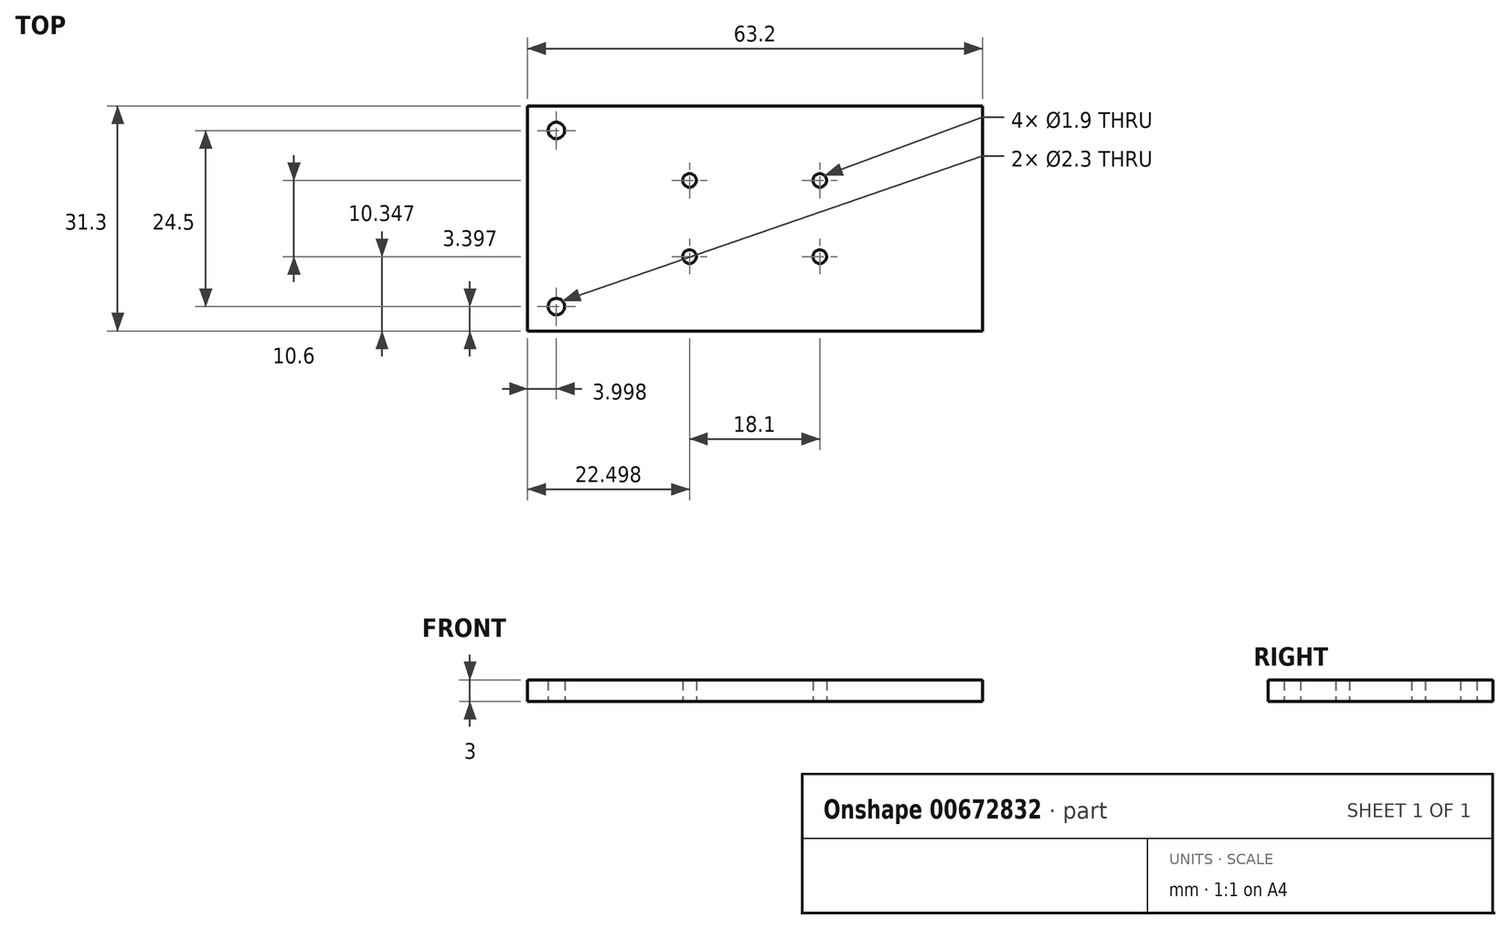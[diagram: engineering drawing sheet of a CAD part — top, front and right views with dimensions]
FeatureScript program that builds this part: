
annotation { "Feature Type Name" : "Feature", "Feature Type Description" : "" }
export const myFeature = defineFeature(function(context is Context, id is Id, definition is map)
    precondition{}
    {
        {
            var Q0;
            Q0=qCreatedBy(makeId("Top.planeOp"),FACE);
            var sketch = newSketch(context, id + "F0", { "sketchPlane" : qUnion([Q0])});
            skLineSegment(sketch, "E0.bottom", {"start": v(-37.93, -0.11) * mm, "end": v(25.27, -0.11) * mm});
            skLineSegment(sketch, "E0.top", {"start": v(-37.93, -15.76) * mm, "end": v(25.27, -15.76) * mm});
            skLineSegment(sketch, "E0.left", {"start": v(-37.93, -0.11) * mm, "end": v(-37.93, -15.76) * mm});
            skLineSegment(sketch, "E0.right", {"start": v(25.27, -0.11) * mm, "end": v(25.27, -15.76) * mm});
            skLineSegment(sketch, "E1", {"start": v(-33.93, -0.11) * mm, "end": v(-33.93, -3.51) * mm});
            skLineSegment(sketch, "E2", {"start": v(-33.93, -3.51) * mm, "end": v(-37.93, -3.51) * mm});
            skCircle(sketch, "E3", {"center": v(-33.93, -3.51) * mm, "radius": 1.15 * mm});
            skLineSegment(sketch, "E4", {"start": v(-37.93, -10.46) * mm, "end": v(-15.43, -10.46) * mm});
            skLineSegment(sketch, "E5", {"start": v(-15.43, -10.46) * mm, "end": v(2.67, -10.46) * mm});
            skLineSegment(sketch, "E6", {"start": v(-5.3, -10.46) * mm, "end": v(-5.3, -15.76) * mm});
            skCircle(sketch, "E7", {"center": v(-15.43, -10.46) * mm, "radius": 0.95 * mm});
            skCircle(sketch, "E8", {"center": v(2.67, -10.46) * mm, "radius": 0.95 * mm});
            skSolve(sketch);
        }
        {
            var Q0;
            {var subQ13=sQuery(id+"F0.wireOp",EDGE,"E0.right");Q0=makeQuery(id+"F0.imprint","IMPRINT",FACE,{"disambiguationData":[TD([[makeQuery(id+"F0.imprint","IMPRINT",EDGE,{"derivedFrom":subQ13}),-1.0]])]});}
            var Q1;
            {var subQ1=sQuery(id+"F0.wireOp",EDGE,"E0.left");var subQ5=sQuery(id+"F0.wireOp",EDGE,"E0.bottom");var subQ6=makeQuery(id+"F0.imprint","INTERSECT",VERTEX,{"derivedFrom":[subQ5,subQ1]});Q1=makeQuery(id+"F0.imprint","IMPRINT",FACE,{"disambiguationData":[TD([[makeQuery(id+"F0.imprint","IMPRINT",EDGE,{"disambiguationData":[TD([[subQ6,-1.0]])],"derivedFrom":subQ5}),-1.0]])]});}
            var Q2;
            {var subQ7=sQuery(id+"F0.wireOp",EDGE,"E6");Q2=makeQuery(id+"F0.imprint","IMPRINT",FACE,{"disambiguationData":[TD([[makeQuery(id+"F0.imprint","IMPRINT",EDGE,{"derivedFrom":subQ7}),-1.0]])]});}
            extrude(context, id + "F1", {"entities" : qUnion([Q0, Q1, Q2]), "depth" : 3 * mm, "offsetDistance" : 25 * mm});
        }
        {
            var Q0;
            Q0=makeQuery(id+"F1.opExtrude","SWEPT_BODY",BODY,{"disambiguationData":[OSD([sQuery(id+"F0.wireOp",EDGE,"E0.bottom"),sQuery(id+"F0.wireOp",EDGE,"E0.top"),sQuery(id+"F0.wireOp",EDGE,"E0.left"),sQuery(id+"F0.wireOp",EDGE,"E0.right"),sQuery(id+"F0.wireOp",EDGE,"E3"),sQuery(id+"F0.wireOp",EDGE,"E7"),sQuery(id+"F0.wireOp",EDGE,"E8")])]});
            var Q1;
            Q1=makeQuery(id+"F1.opExtrude","SWEPT_FACE",FACE,{"disambiguationData":[OSD([sQuery(id+"F0.wireOp",EDGE,"E0.top")])]});
            mirror(context, id + "F2", {"operationType" : NewBodyOperationType.ADD, "entities" : qUnion([Q0]), "mirrorPlane" : qUnion([Q1])});
        }
    });
